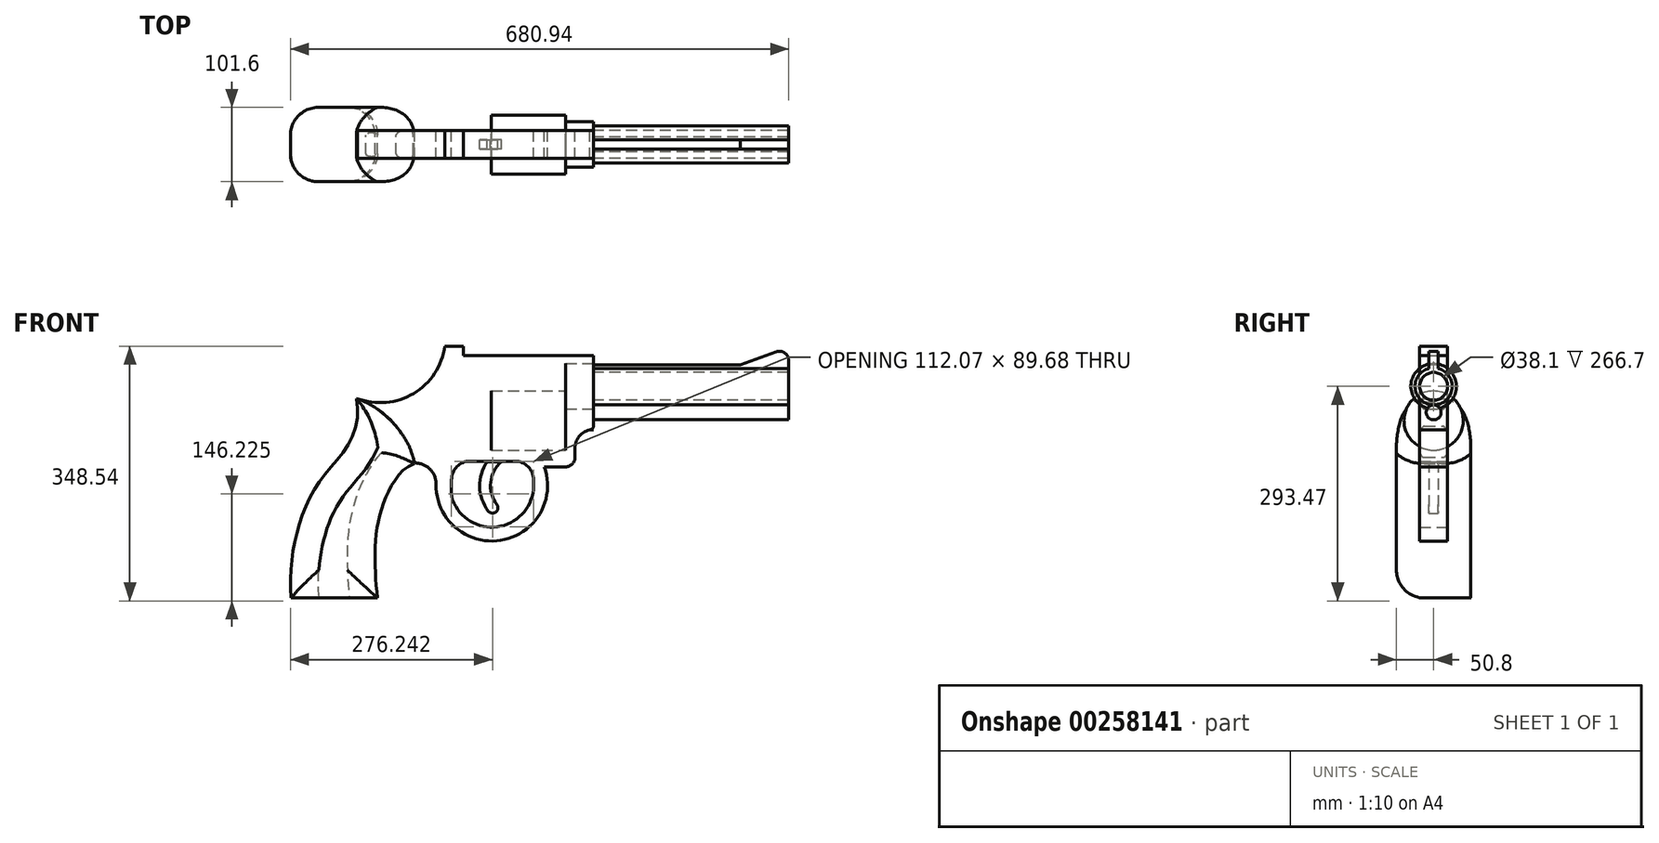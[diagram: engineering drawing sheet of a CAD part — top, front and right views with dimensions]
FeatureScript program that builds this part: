
annotation { "Feature Type Name" : "Feature", "Feature Type Description" : "" }
export const myFeature = defineFeature(function(context is Context, id is Id, definition is map)
    precondition{}
    {
        {
            var Q0;
            Q0=qCreatedBy(makeId("Right.planeOp"),FACE);
            var sketch = newSketch(context, id + "F0", { "sketchPlane" : qUnion([Q0])});
            skArc(sketch, "E0", {"start": v(-6.35, 265.9) * mm, "mid": v(0, 215.9) * mm, "end": v(6.35, 265.9) * mm});
            skCircle(sketch, "E1.0", {"center": v(0, 241.3) * mm, "radius": 19.05 * mm});
            skCircle(sketch, "E2", {"center": v(0, 205.74) * mm, "radius": 10.16 * mm});
            skLineSegment(sketch, "E3", {"start": v(-6.35, 265.9) * mm, "end": v(-6.35, 270.97) * mm});
            skLineSegment(sketch, "E4", {"start": v(-6.35, 270.97) * mm, "end": v(6.35, 270.97) * mm});
            skLineSegment(sketch, "E5", {"start": v(6.35, 270.97) * mm, "end": v(6.35, 265.9) * mm});
            skSolve(sketch);
        }
        {
            var Q0;
            Q0=makeQuery(id+"F0.imprint","IMPRINT",FACE,{"disambiguationData":[TD([[makeQuery(id+"F0.imprint","IMPRINT",EDGE,{"derivedFrom":sQuery(id+"F0.wireOp",EDGE,"E1.0")}),-1.0]])]});
            var Q1;
            Q1=makeQuery(id+"F0.imprint","IMPRINT",FACE,{"disambiguationData":[TD([[makeQuery(id+"F0.imprint","IMPRINT",EDGE,{"derivedFrom":sQuery(id+"F0.wireOp",EDGE,"E2")}),1.0]])]});
            extrude(context, id + "F1", {"entities" : qUnion([Q0, Q1]), "depth" : 215.9 * mm, "hasSecondDirection" : true, "secondDirectionOppositeDirection" : true, "secondDirectionDepth" : 50.8 * mm});
        }
        {
            var Q0;
            Q0=qCreatedBy(makeId("Front.planeOp"),FACE);
            var sketch = newSketch(context, id + "F2", { "sketchPlane" : qUnion([Q0])});
            skLineSegment(sketch, "E6", {"start": v(215.9, 270.97) * mm, "end": v(215.9, 276.75) * mm});
            skLineSegment(sketch, "E7", {"start": v(198.86, 288.68) * mm, "end": v(150.16, 270.97) * mm});
            skLineSegment(sketch, "E8", {"start": v(150.16, 270.97) * mm, "end": v(215.9, 270.97) * mm});
            skPoint(sketch, "E9.visualSharp", {"position": v(215.9, 294.88) * mm});
            skArc(sketch, "E9.filletArc", {"start": v(215.9, 276.75) * mm, "mid": v(210.49, 287.15) * mm, "end": v(198.86, 288.68) * mm});
            skSolve(sketch);
        }
        {
            var Q0;
            Q0=qSketchRegion(id+"F2",true);
            extrude(context, id + "F3", {"entities" : qUnion([Q0]), "operationType" : NewBodyOperationType.ADD, "oppositeDirection" : true, "depth" : 6.35 * mm, "hasSecondDirection" : true, "secondDirectionOppositeDirection" : false, "secondDirectionDepth" : 6.35 * mm});
        }
        {
            var Q0;
            Q0=qCreatedBy(makeId("Front.planeOp"),FACE);
            var sketch = newSketch(context, id + "F4", { "sketchPlane" : qUnion([Q0])});
            skLineSegment(sketch, "E10", {"start": v(-50.8, 270.97) * mm, "end": v(-50.8, 187.15) * mm});
            skLineSegment(sketch, "E11", {"start": v(-50.8, 182.07) * mm, "end": v(-55.88, 182.07) * mm});
            skLineSegment(sketch, "E12", {"start": v(-76.2, 156.67) * mm, "end": v(-76.2, 143.97) * mm});
            skLineSegment(sketch, "E13", {"start": v(-88.9, 131.27) * mm, "end": v(-117.91, 131.27) * mm});
            skPoint(sketch, "E14.visualSharp", {"position": v(-50.8, 182.07) * mm});
            skArc(sketch, "E14.filletArc", {"start": v(-55.88, 182.07) * mm, "mid": v(-52.29, 183.56) * mm, "end": v(-50.8, 187.15) * mm});
            skPoint(sketch, "E15.visualSharp", {"position": v(-76.2, 182.07) * mm});
            skArc(sketch, "E15.filletArc", {"start": v(-50.8, 182.07) * mm, "mid": v(-68.76, 174.63) * mm, "end": v(-76.2, 156.67) * mm});
            skPoint(sketch, "E16.visualSharp", {"position": v(-76.2, 131.27) * mm});
            skArc(sketch, "E16.filletArc", {"start": v(-88.9, 131.27) * mm, "mid": v(-79.92, 135) * mm, "end": v(-76.2, 143.97) * mm});
            skArc(sketch, "E17", {"start": v(-265.94, 107.45) * mm, "mid": v(-178.49, 30.51) * mm, "end": v(-117.36, 129.67) * mm});
            skArc(sketch, "E18", {"start": v(-243.18, 85.59) * mm, "mid": v(-182.27, 49.22) * mm, "end": v(-132.89, 100.16) * mm});
            skArc(sketch, "E19", {"start": v(-265.94, 107.45) * mm, "mid": v(-274.3, 128.17) * mm, "end": v(-295.08, 136.4) * mm});
            skLineSegment(sketch, "E20.bottom", {"start": v(-242.81, 101.61) * mm, "end": v(-246.74, 101.61) * mm});
            skLineSegment(sketch, "E20.top", {"start": v(-158.16, 138.9) * mm, "end": v(-219.44, 138.9) * mm});
            skLineSegment(sketch, "E20.left", {"start": v(-132.76, 102.7) * mm, "end": v(-132.76, 113.5) * mm});
            skLineSegment(sketch, "E20.right", {"start": v(-244.84, 94.6) * mm, "end": v(-244.84, 113.5) * mm});
            skArc(sketch, "E21.filletArc", {"start": v(-219.44, 138.9) * mm, "mid": v(-237.4, 131.45) * mm, "end": v(-244.84, 113.5) * mm});
            skArc(sketch, "E22.filletArc", {"start": v(-132.76, 113.5) * mm, "mid": v(-140.2, 131.45) * mm, "end": v(-158.16, 138.9) * mm});
            skArc(sketch, "E23.trimOffspring", {"start": v(-265.94, 107.45) * mm, "mid": v(-177.65, 30.64) * mm, "end": v(-117.91, 131.27) * mm});
            skArc(sketch, "E24.filletArc", {"start": v(-244.84, 94.6) * mm, "mid": v(-244.42, 90.02) * mm, "end": v(-243.18, 85.59) * mm});
            skPoint(sketch, "E25.visualSharp", {"position": v(-132.76, 101.61) * mm});
            skArc(sketch, "E25.filletArc", {"start": v(-132.89, 100.16) * mm, "mid": v(-132.8, 101.43) * mm, "end": v(-132.76, 102.7) * mm});
            skArc(sketch, "E26", {"start": v(-295.08, 136.4) * mm, "mid": v(-323.42, 190.23) * mm, "end": v(-373.53, 224.7) * mm});
            skArc(sketch, "E27", {"start": v(-373.53, 224.7) * mm, "mid": v(-296.43, 231.64) * mm, "end": v(-254, 296.37) * mm});
            skLineSegment(sketch, "E28", {"start": v(-254, 296.37) * mm, "end": v(-228.6, 296.37) * mm});
            skLineSegment(sketch, "E29", {"start": v(-228.6, 296.37) * mm, "end": v(-228.6, 283.67) * mm});
            skLineSegment(sketch, "E30", {"start": v(-228.6, 283.67) * mm, "end": v(-50.8, 283.67) * mm});
            skLineSegment(sketch, "E31", {"start": v(-50.8, 283.67) * mm, "end": v(-50.8, 270.97) * mm});
            skSolve(sketch);
        }
        {
            var Q0;
            Q0=qSketchRegion(id+"F4",true);
            var Q1;
            Q1=makeQuery(id+"F4.imprint","IMPRINT",FACE,{"disambiguationData":[TD([[makeQuery(id+"F4.imprint","IMPRINT",EDGE,{"derivedFrom":sQuery(id+"F4.wireOp",EDGE,"E10")}),-1.0]])]});
            extrude(context, id + "F5", {"entities" : qUnion([Q0, Q1]), "depth" : 19.05 * mm, "hasSecondDirection" : true, "secondDirectionOppositeDirection" : true, "secondDirectionDepth" : 19.05 * mm});
        }
        {
            var Q0;
            Q0=qCreatedBy(makeId("Front.planeOp"),FACE);
            var sketch = newSketch(context, id + "F6", { "sketchPlane" : qUnion([Q0])});
            skArc(sketch, "E32", {"start": v(-176.64, 138.15) * mm, "mid": v(-191.33, 110.15) * mm, "end": v(-182.84, 79.7) * mm});
            skArc(sketch, "E33", {"start": v(-196.32, 138.15) * mm, "mid": v(-206.34, 104.18) * mm, "end": v(-194.61, 70.75) * mm});
            skArc(sketch, "E34", {"start": v(-194.61, 70.75) * mm, "mid": v(-184.25, 69.34) * mm, "end": v(-182.84, 79.7) * mm});
            skLineSegment(sketch, "E35", {"start": v(-176.64, 138.15) * mm, "end": v(-196.32, 138.15) * mm});
            skSolve(sketch);
        }
        {
            var Q0;
            Q0=qSketchRegion(id+"F6",true);
            extrude(context, id + "F7", {"entities" : qUnion([Q0]), "depth" : 6.35 * mm, "hasSecondDirection" : true, "secondDirectionOppositeDirection" : true, "secondDirectionDepth" : 6.35 * mm});
        }
        {
            var Q0;
            Q0=qCreatedBy(makeId("Right.planeOp"),FACE);
            var sketch = newSketch(context, id + "F8", { "sketchPlane" : qUnion([Q0])});
            skCircle(sketch, "E36", {"center": v(0, 241.31) * mm, "radius": 31.06 * mm});
            skSolve(sketch);
        }
        {
            var Q0;
            Q0=qSketchRegion(id+"F8",true);
            extrude(context, id + "F9", {"entities" : qUnion([Q0]), "oppositeDirection" : true, "depth" : 38.1 * mm});
        }
        {
            var Q0;
            Q0=makeQuery(id+"F9.opExtrude","SWEPT_BODY",BODY,{"disambiguationData":[OSD([sQuery(id+"F8.wireOp",EDGE,"E36")])]});
            var Q1;
            Q1=qCreatedBy(makeId("Right.planeOp"),FACE);
            transform(context, id + "F10", {"entities" : qUnion([Q0]), "transformType" : TransformType.TRANSLATION_DISTANCE, "transformDirection" : qUnion([Q1]), "distance" : 50.8 * mm, "oppositeDirection" : true, "makeCopy" : false});
        }
        {
            var Q0;
            Q0=qCreatedBy(makeId("Right.planeOp"),FACE);
            var sketch = newSketch(context, id + "F11", { "sketchPlane" : qUnion([Q0])});
            skCircle(sketch, "E37", {"center": v(0, 194.45) * mm, "radius": 40.5 * mm});
            skSolve(sketch);
        }
        {
            var Q0;
            Q0=makeQuery(id+"F11.imprint","IMPRINT",FACE,{"disambiguationData":[TD([[makeQuery(id+"F11.imprint","IMPRINT",EDGE,{"derivedFrom":sQuery(id+"F11.wireOp",EDGE,"E37")}),1.0]])]});
            extrude(context, id + "F12", {"entities" : qUnion([Q0]), "oppositeDirection" : true, "depth" : 101.6 * mm});
        }
        {
            var Q0;
            Q0=makeQuery(id+"F12.opExtrude","SWEPT_BODY",BODY,{"disambiguationData":[OSD([sQuery(id+"F11.wireOp",EDGE,"E37")])]});
            var Q1;
            Q1=qCreatedBy(makeId("Right.planeOp"),FACE);
            transform(context, id + "F13", {"entities" : qUnion([Q0]), "transformType" : TransformType.TRANSLATION_DISTANCE, "transformDirection" : qUnion([Q1]), "distance" : 88.9 * mm, "oppositeDirection" : true, "makeCopy" : false});
        }
        {
            var Q0;
            Q0=qCreatedBy(makeId("Right.planeOp"),FACE);
            var sketch = newSketch(context, id + "F14", { "sketchPlane" : qUnion([Q0])});
            skLineSegment(sketch, "E38", {"start": v(0, 248.2) * mm, "end": v(0, 140.16) * mm, "construction": true});
            skArc(sketch, "E39", {"start": v(0, 153.18) * mm, "mid": v(40.47, 193.65) * mm, "end": v(0, 234.12) * mm});
            skPoint(sketch, "E40.orphan", {"position": v(0, 231.17) * mm});
            skPoint(sketch, "E41.orphan", {"position": v(0, 156.13) * mm});
            skSolve(sketch);
        }
        {
            var Q0;
            Q0=qSketchRegion(id+"F14",true);
            var Q1;
            Q1=sQuery(id+"F14.wireOp",EDGE,"E39");
            var Q2;
            Q2=sQuery(id+"F14.wireOp",EDGE,"E38");
            revolve(context, id + "F15", {"bodyType" : ToolBodyType.SURFACE, "entities" : qUnion([Q0]), "surfaceEntities" : qUnion([Q1]), "axis" : qUnion([Q2]), "revolveType" : RevolveType.ONE_DIRECTION, "oppositeDirection" : true, "angle" : 180 * degree});
        }
        {
            var Q0;
            Q0=makeQuery(id+"F15.opRevolve","SWEPT_BODY",BODY,{"disambiguationData":[OSD([sQuery(id+"F14.wireOp",EDGE,"E39")])]});
            var Q1;
            Q1=qCreatedBy(makeId("Right.planeOp"),FACE);
            transform(context, id + "F16", {"entities" : qUnion([Q0]), "transformType" : TransformType.TRANSLATION_DISTANCE, "transformDirection" : qUnion([Q1]), "distance" : 203.2 * mm, "oppositeDirection" : true, "makeCopy" : false});
        }
        {
            var Q0;
            Q0=makeQuery(id+"F15.opRevolve","SWEPT_BODY",BODY,{"disambiguationData":[OSD([sQuery(id+"F14.wireOp",EDGE,"E39")])]});
            var Q1;
            Q1=qCreatedBy(makeId("Right.planeOp"),FACE);
            transform(context, id + "F17", {"entities" : qUnion([Q0]), "transformType" : TransformType.TRANSLATION_DISTANCE, "transformDirection" : qUnion([Q1]), "distance" : 12.7 * mm, "makeCopy" : false});
        }
        {
            var Q0;
            Q0=makeQuery(id+"F15.opRevolve","SWEPT_BODY",BODY,{"disambiguationData":[OSD([sQuery(id+"F14.wireOp",EDGE,"E39")])]});
            var Q1;
            Q1=qCreatedBy(makeId("Right.planeOp"),FACE);
            transform(context, id + "F18", {"entities" : qUnion([Q0]), "transformType" : TransformType.TRANSLATION_DISTANCE, "transformDirection" : qUnion([Q1]), "distance" : 6.35 * mm, "oppositeDirection" : true, "makeCopy" : false});
        }
        {
            var Q0;
            Q0=qCreatedBy(makeId("Front.planeOp"),FACE);
            var sketch = newSketch(context, id + "F19", { "sketchPlane" : qUnion([Q0])});
            skFitSpline(sketch, "E42", {"points": [v(-295.97, 135.37) * mm, v(-315.66, 121.53) * mm, v(-342.8, 65.11) * mm, v(-349.2, 0) * mm, v(-346, -48.26) * mm], "startDerivative": vector(-116.91, -52.78) * mm, "endDerivative": vector(18.49, -146.52) * mm});
            skFitSpline(sketch, "E43", {"points": [v(-374.74, 224.25) * mm, v(-374.21, 193.38) * mm, v(-388.05, 158.26) * mm, v(-413.74, 126.05) * mm, v(-448.96, 64.85) * mm, v(-463.97, -47.74) * mm], "startDerivative": vector(25.4, -198.34) * mm, "endDerivative": vector(39.5, -350.92) * mm});
            skLineSegment(sketch, "E44", {"start": v(-463.97, -47.74) * mm, "end": v(-346, -48.26) * mm});
            skFitSpline(sketch, "E45", {"points": [v(-374.74, 224.25) * mm, v(-332.33, 198.8) * mm, v(-295.97, 135.37) * mm], "startDerivative": vector(113.06, -31.02) * mm, "endDerivative": vector(12.54, -151.1) * mm});
            skSolve(sketch);
        }
        {
            var Q0;
            Q0=makeQuery(id+"F19.imprint","IMPRINT",FACE,{"disambiguationData":[TD([[makeQuery(id+"F19.imprint","IMPRINT",EDGE,{"derivedFrom":sQuery(id+"F19.wireOp",EDGE,"E42")}),-1.0]])]});
            extrude(context, id + "F20", {"entities" : qUnion([Q0]), "operationType" : NewBodyOperationType.ADD, "depth" : 50.8 * mm, "hasSecondDirection" : true, "secondDirectionOppositeDirection" : true, "secondDirectionDepth" : 50.8 * mm});
        }
        {
            var Q0;
            Q0=makeQuery(id+"F20.opExtrude","CAP_EDGE",EDGE,{"disambiguationData":[OSD([sQuery(id+"F19.wireOp",EDGE,"E43")])],"isStart":true});
            var Q1;
            Q1=makeQuery(id+"F20.opExtrude","CAP_EDGE",EDGE,{"disambiguationData":[OSD([sQuery(id+"F19.wireOp",EDGE,"E45")])],"isStart":true});
            var Q2;
            Q2=makeQuery(id+"F20.opExtrude","CAP_EDGE",EDGE,{"disambiguationData":[OSD([sQuery(id+"F19.wireOp",EDGE,"E42")])],"isStart":true});
            var Q3;
            Q3=makeQuery(id+"F20.opExtrude","CAP_EDGE",EDGE,{"disambiguationData":[OSD([sQuery(id+"F19.wireOp",EDGE,"E43")])],"isStart":false});
            var Q4;
            Q4=makeQuery(id+"F20.opExtrude","CAP_FACE",FACE,{"disambiguationData":[OSD([sQuery(id+"F19.wireOp",EDGE,"E42"),sQuery(id+"F19.wireOp",EDGE,"E43"),sQuery(id+"F19.wireOp",EDGE,"E44"),sQuery(id+"F19.wireOp",EDGE,"E45")])],"isStart":false});
            var Q5;
            Q5=makeQuery(id+"F20.opExtrude","CAP_EDGE",EDGE,{"disambiguationData":[OSD([sQuery(id+"F19.wireOp",EDGE,"E42")])],"isStart":false});
            fillet(context, id + "F21", {"entities" : qUnion([Q0, Q1, Q2, Q3, Q4, Q5]), "radius" : 38.1 * mm, "tangentPropagation" : true, "allowEdgeOverflow" : false});
        }
    });
